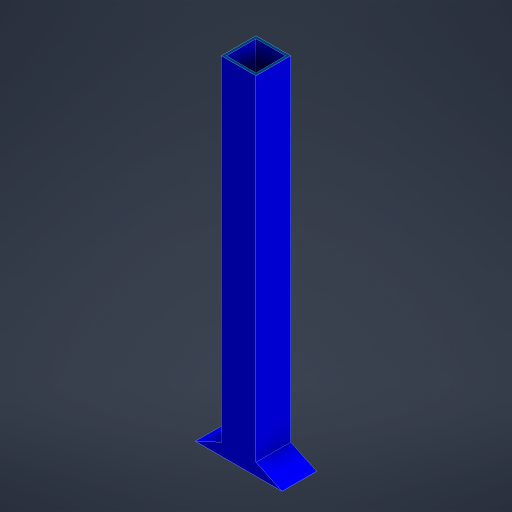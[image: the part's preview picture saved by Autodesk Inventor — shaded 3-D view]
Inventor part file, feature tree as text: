
AUTODESK INVENTOR PART (.ipt)
format: ipt  version: 2024 (Build 280153000, 153)  size: 208,896 bytes
history: native  units: mm
features: other x5, extrude x1, sketch x1, projected_geometry x1
ambient origin geometry x8: Origin, YZ Plane, XZ Plane, XY Plane, X Axis, Y Axis, Z Axis, Center Point
bodies: Body1 (feature_tree)
feature tree (8):
  other  "shock_absorber_holder_down_150.ipt"
  extrude  "Выдавливание1"  Depth=10.0mm
  other  "Твердое тело1::shock_absorber_holder_down_150.ipt"
  other  "Элемент создания тегов1"
  other  "РабПлоскость1"
  sketch  "Эскиз1"
  projected_geometry  "Спроецированная петля1"
  other  "Твердое тело1"
